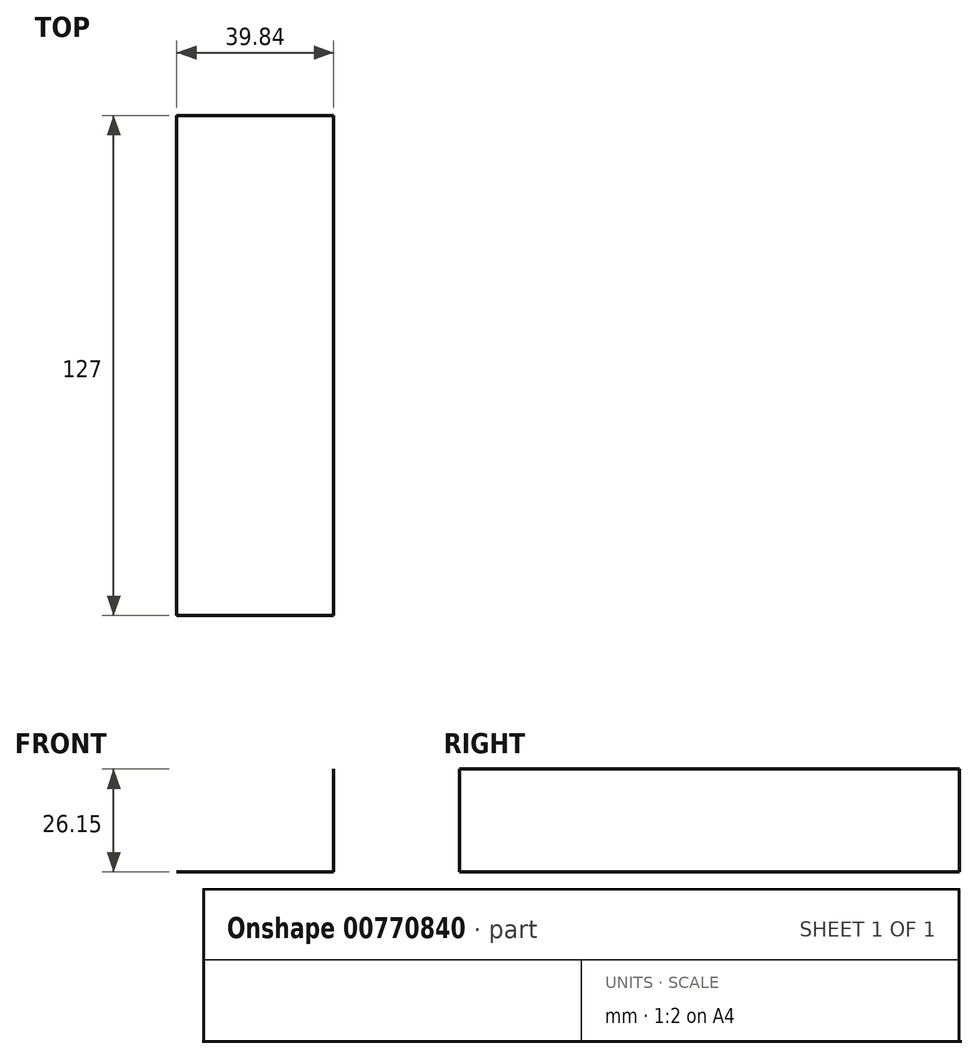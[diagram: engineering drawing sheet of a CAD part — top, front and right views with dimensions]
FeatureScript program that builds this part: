
annotation { "Feature Type Name" : "Feature", "Feature Type Description" : "" }
export const myFeature = defineFeature(function(context is Context, id is Id, definition is map)
    precondition{}
    {
        {
            var Q0;
            Q0=qCreatedBy(makeId("Front.planeOp"),FACE);
            var sketch = newSketch(context, id + "F0", { "sketchPlane" : qUnion([Q0])});
            skLineSegment(sketch, "E0", {"start": v(-39.84, 0) * mm, "end": v(0, 0) * mm});
            skLineSegment(sketch, "E1", {"start": v(0, 0) * mm, "end": v(0, 26.15) * mm});
            skSolve(sketch);
        }
        {
            var Q0;
            Q0=sQuery(id+"F0.wireOp",EDGE,"E1");
            var Q1;
            Q1=sQuery(id+"F0.wireOp",EDGE,"E0");
            extrude(context, id + "F1", {"bodyType" : ToolBodyType.SURFACE, "surfaceEntities" : qUnion([Q0, Q1]), "depth" : 127 * mm, "offsetDistance" : 25.4 * mm});
        }
    });
